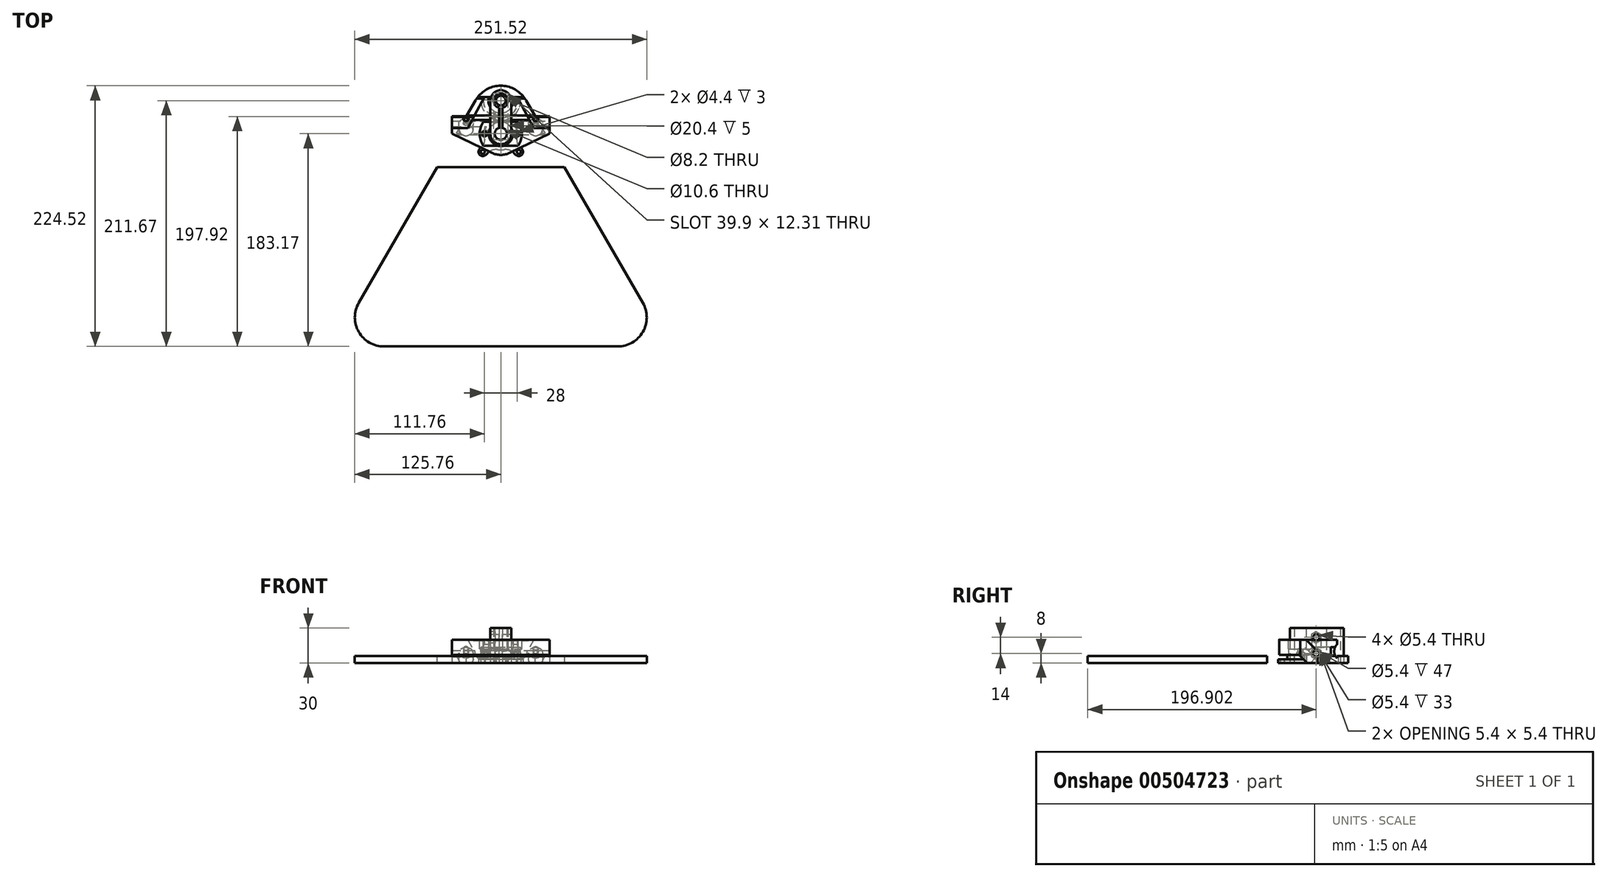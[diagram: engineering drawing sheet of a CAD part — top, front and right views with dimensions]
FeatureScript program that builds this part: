
annotation { "Feature Type Name" : "Feature", "Feature Type Description" : "" }
export const myFeature = defineFeature(function(context is Context, id is Id, definition is map)
    precondition{}
    {
        {
            var Q0;
            Q0=qCreatedBy(makeId("Top.planeOp"),FACE);
            var sketch = newSketch(context, id + "F0", { "sketchPlane" : qUnion([Q0])});
            skCircle(sketch, "E0.cCircle", {"center": v(0, 100) * mm, "radius": 15.5 * mm, "construction": true});
            skLineSegment(sketch, "E0.0", {"start": v(15.5, 115.5) * mm, "end": v(15.5, 84.5) * mm, "construction": true});
            skLineSegment(sketch, "E0.1", {"start": v(15.5, 84.5) * mm, "end": v(-15.5, 84.5) * mm, "construction": true});
            skLineSegment(sketch, "E0.2", {"start": v(-15.5, 84.5) * mm, "end": v(-15.5, 115.5) * mm, "construction": true});
            skLineSegment(sketch, "E0.3", {"start": v(-15.5, 115.5) * mm, "end": v(15.5, 115.5) * mm, "construction": true});
            skPoint(sketch, "E0.0.midPoint", {"position": v(15.5, 100) * mm});
            skCircle(sketch, "E1", {"center": v(0, 100) * mm, "radius": 11.1 * mm});
            skCircle(sketch, "E2", {"center": v(-15.5, 115.5) * mm, "radius": 1.7 * mm});
            skCircle(sketch, "E3", {"center": v(15.5, 115.5) * mm, "radius": 1.7 * mm});
            skCircle(sketch, "E4", {"center": v(15.5, 84.5) * mm, "radius": 1.7 * mm});
            skCircle(sketch, "E5", {"center": v(-15.5, 84.5) * mm, "radius": 1.7 * mm});
            skCircle(sketch, "E6.cCircle", {"center": v(0, 128.5) * mm, "radius": 6.5 * mm, "construction": true});
            skLineSegment(sketch, "E6.0", {"start": v(3.75, 122) * mm, "end": v(-3.75, 122) * mm, "construction": true});
            skLineSegment(sketch, "E6.1", {"start": v(-3.75, 122) * mm, "end": v(-7.5, 128.5) * mm, "construction": true});
            skLineSegment(sketch, "E6.2", {"start": v(-7.5, 128.5) * mm, "end": v(-3.75, 135) * mm, "construction": true});
            skLineSegment(sketch, "E6.3", {"start": v(-3.75, 135) * mm, "end": v(3.75, 135) * mm, "construction": true});
            skLineSegment(sketch, "E6.4", {"start": v(3.75, 135) * mm, "end": v(7.5, 128.5) * mm, "construction": true});
            skLineSegment(sketch, "E6.5", {"start": v(7.5, 128.5) * mm, "end": v(3.75, 122) * mm, "construction": true});
            skPoint(sketch, "E6.0.midPoint", {"position": v(0, 122) * mm});
            skCircle(sketch, "E7", {"center": v(0, 128.5) * mm, "radius": 4.1 * mm});
            skSolve(sketch);
        }
        {
            var Q0;
            Q0=qCreatedBy(makeId("Top.planeOp"),FACE);
            var sketch = newSketch(context, id + "F1", { "sketchPlane" : qUnion([Q0])});
            skCircle(sketch, "E8.cCircle", {"center": v(0, 0) * mm, "radius": 83.17 * mm, "construction": true});
            skLineSegment(sketch, "E8.0", {"start": v(144.06, -83.17) * mm, "end": v(-144.06, -83.17) * mm});
            skLineSegment(sketch, "E8.1", {"start": v(-144.06, -83.17) * mm, "end": v(0, 166.35) * mm});
            skLineSegment(sketch, "E8.2", {"start": v(0, 166.35) * mm, "end": v(144.06, -83.17) * mm});
            skPoint(sketch, "E8.0.midPoint", {"position": v(0, -83.17) * mm});
            skSolve(sketch);
        }
        {
            var Q0;
            Q0=qSketchRegion(id+"F1",true);
            extrude(context, id + "F2", {"entities" : qUnion([Q0]), "depth" : 6 * mm});
        }
        {
            var Q0;
            Q0=qSketchRegion(id+"F0",true);
            extrude(context, id + "F3", {"entities" : qUnion([Q0]), "operationType" : NewBodyOperationType.REMOVE, "endBound" : BoundingType.THROUGH_ALL, "depth" : 25 * mm});
        }
        {
            var Q0;
            Q0=qCreatedBy(makeId("Front.planeOp"),FACE);
            var sketch = newSketch(context, id + "F4", { "sketchPlane" : qUnion([Q0])});
            skLineSegment(sketch, "E9", {"start": v(0, 0) * mm, "end": v(0, 150.06) * mm, "construction": true});
            skSolve(sketch);
        }
        {
            var Q0;
            Q0=makeQuery(id+"F2.opExtrude","SWEPT_EDGE",EDGE,{"disambiguationData":[OSD([sQuery(id+"F1.wireOp",EDGE,"E8.0"),sQuery(id+"F1.wireOp",EDGE,"E8.1")])]});
            var Q1;
            Q1=makeQuery(id+"F2.opExtrude","SWEPT_EDGE",EDGE,{"disambiguationData":[OSD([sQuery(id+"F1.wireOp",EDGE,"E8.0"),sQuery(id+"F1.wireOp",EDGE,"E8.2")])]});
            var Q2;
            Q2=makeQuery(id+"F2.opExtrude","SWEPT_EDGE",EDGE,{"disambiguationData":[OSD([sQuery(id+"F1.wireOp",EDGE,"E8.1"),sQuery(id+"F1.wireOp",EDGE,"E8.2")])]});
            fillet(context, id + "F5", {"entities" : qUnion([Q0, Q1, Q2]), "radius" : 25 * mm, "tangentPropagation" : true, "allowEdgeOverflow" : false});
        }
        {
            var Q0;
            Q0=qCreatedBy(makeId("Top.planeOp"),FACE);
            var sketch = newSketch(context, id + "F6", { "sketchPlane" : qUnion([Q0])});
            skArc(sketch, "E10", {"start": v(-10.2, 131.73) * mm, "mid": v(0, 117.8) * mm, "end": v(10.2, 131.73) * mm});
            skCircle(sketch, "E11", {"center": v(0, 100) * mm, "radius": 10.2 * mm});
            skLineSegment(sketch, "E12", {"start": v(-14, 100) * mm, "end": v(14, 100) * mm, "construction": true});
            skCircle(sketch, "E13", {"center": v(14, 100) * mm, "radius": 2.2 * mm});
            skCircle(sketch, "E14", {"center": v(-14, 100) * mm, "radius": 2.2 * mm});
            skLineSegment(sketch, "E15", {"start": v(-30, 100) * mm, "end": v(30, 100) * mm, "construction": true});
            skArc(sketch, "E16", {"start": v(9.53, 136.9) * mm, "mid": v(0, 141.2) * mm, "end": v(-9.53, 136.9) * mm, "construction": true});
            skLineSegment(sketch, "E17", {"start": v(-30, 100) * mm, "end": v(-42, 100) * mm, "construction": true});
            skLineSegment(sketch, "E18", {"start": v(30, 100) * mm, "end": v(42, 100) * mm, "construction": true});
            skCircle(sketch, "E19", {"center": v(-30, 100) * mm, "radius": 6 * mm, "construction": true});
            skCircle(sketch, "E20", {"center": v(30, 100) * mm, "radius": 6 * mm, "construction": true});
            skLineSegment(sketch, "E21", {"start": v(-14.07, 131.73) * mm, "end": v(-42, 100) * mm, "construction": true});
            skLineSegment(sketch, "E22", {"start": v(14.07, 131.73) * mm, "end": v(42, 100) * mm, "construction": true});
            skArc(sketch, "E23", {"start": v(-7.89, 83.6) * mm, "mid": v(0, 81.8) * mm, "end": v(7.89, 83.6) * mm});
            skLineSegment(sketch, "E24", {"start": v(-7.89, 83.6) * mm, "end": v(-42, 100) * mm});
            skLineSegment(sketch, "E25", {"start": v(42, 100) * mm, "end": v(7.89, 83.6) * mm});
            skLineSegment(sketch, "E26", {"start": v(10.2, 131.73) * mm, "end": v(14.07, 131.73) * mm});
            skLineSegment(sketch, "E27", {"start": v(-10.2, 131.73) * mm, "end": v(-14.07, 131.73) * mm});
            skPoint(sketch, "E28", {"position": v(10.7, 128.5) * mm});
            skLineSegment(sketch, "E29", {"start": v(42, 100) * mm, "end": v(42, 115) * mm});
            skLineSegment(sketch, "E30", {"start": v(42, 115) * mm, "end": v(23, 115) * mm});
            skLineSegment(sketch, "E31", {"start": v(23, 115) * mm, "end": v(14.07, 131.73) * mm});
            skLineSegment(sketch, "E32", {"start": v(-42, 100) * mm, "end": v(-42, 115) * mm});
            skLineSegment(sketch, "E33", {"start": v(-42, 115) * mm, "end": v(-23, 115) * mm});
            skLineSegment(sketch, "E34", {"start": v(-23, 115) * mm, "end": v(-14.07, 131.73) * mm});
            skSolve(sketch);
        }
        {
            var Q0;
            Q0=qSketchRegion(id+"F6",true);
            extrude(context, id + "F7", {"entities" : qUnion([Q0]), "depth" : 20 * mm});
        }
        {
            var Q0;
            Q0=makeQuery(id+"F7.opExtrude","CAP_FACE",FACE,{"disambiguationData":[OSD([sQuery(id+"F6.wireOp",EDGE,"E10"),sQuery(id+"F6.wireOp",EDGE,"E11"),sQuery(id+"F6.wireOp",EDGE,"E13"),sQuery(id+"F6.wireOp",EDGE,"E14"),sQuery(id+"F6.wireOp",EDGE,"E16"),sQuery(id+"F6.wireOp",EDGE,"E21"),sQuery(id+"F6.wireOp",EDGE,"E22"),sQuery(id+"F6.wireOp",EDGE,"E23"),sQuery(id+"F6.wireOp",EDGE,"E24"),sQuery(id+"F6.wireOp",EDGE,"E25")])],"isStart":false});
            var sketch = newSketch(context, id + "F8", { "sketchPlane" : qUnion([Q0])});
            skLineSegment(sketch, "E35", {"start": v(-15.07, 89.8) * mm, "end": v(15.07, 89.8) * mm});
            skLineSegment(sketch, "E36", {"start": v(-15.07, 110.2) * mm, "end": v(15.07, 110.2) * mm});
            skArc(sketch, "E37", {"start": v(-15.07, 110.2) * mm, "mid": v(-18.2, 100) * mm, "end": v(-15.07, 89.8) * mm});
            skArc(sketch, "E38", {"start": v(15.07, 89.8) * mm, "mid": v(18.2, 100) * mm, "end": v(15.07, 110.2) * mm});
            skLineSegment(sketch, "E39", {"start": v(-15.07, 89.8) * mm, "end": v(-15.07, 110.2) * mm, "construction": true});
            skPoint(sketch, "E40", {"position": v(-15.07, 100) * mm});
            skSolve(sketch);
        }
        {
            var Q0;
            Q0=qSketchRegion(id+"F8",true);
            extrude(context, id + "F9", {"entities" : qUnion([Q0]), "operationType" : NewBodyOperationType.REMOVE, "oppositeDirection" : true, "depth" : 8 * mm});
        }
        {
            var Q0;
            Q0=qCreatedBy(makeId("Right.planeOp"),FACE);
            var Q1;
            Q1=sQuery(id+"F6.wireOp",VERTEX,"E18.start");
            cPlane(context, id + "F10", {"entities" : qUnion([Q0, Q1]), "cplaneType" : CPlaneType.PLANE_POINT, "offset" : 25 * mm, "width" : 150 * mm, "height" : 150 * mm});
        }
        {
            var Q0;
            Q0=qCreatedBy(id+"F10.planeOp",FACE);
            var sketch = newSketch(context, id + "F11", { "sketchPlane" : qUnion([Q0])});
            skLineSegment(sketch, "E41", {"start": v(100, 0) * mm, "end": v(100, 22.3) * mm, "construction": true});
            skLineSegment(sketch, "E42", {"start": v(123.17, 29.23) * mm, "end": v(76.83, -17.1) * mm, "construction": true});
            skPoint(sketch, "E43", {"position": v(100, 6.06) * mm});
            skCircle(sketch, "E44", {"center": v(100, 6.06) * mm, "radius": 5 * mm, "construction": true});
            skLineSegment(sketch, "E45", {"start": v(99.34, 11.06) * mm, "end": v(102.07, 11.06) * mm, "construction": true});
            skLineSegment(sketch, "E46", {"start": v(102.07, 11.06) * mm, "end": v(105, 8.13) * mm, "construction": true});
            skLineSegment(sketch, "E47", {"start": v(105, 8.13) * mm, "end": v(105, 5.4) * mm, "construction": true});
            skLineSegment(sketch, "E48", {"start": v(99.34, 11.06) * mm, "end": v(97.93, 12.47) * mm, "construction": true});
            skLineSegment(sketch, "E49", {"start": v(97.93, 12.47) * mm, "end": v(101.46, 16.01) * mm, "construction": true});
            skLineSegment(sketch, "E50", {"start": v(101.46, 16.01) * mm, "end": v(109.95, 7.53) * mm, "construction": true});
            skLineSegment(sketch, "E51", {"start": v(109.95, 7.53) * mm, "end": v(106.41, 3.99) * mm, "construction": true});
            skLineSegment(sketch, "E52", {"start": v(106.41, 3.99) * mm, "end": v(105, 5.4) * mm, "construction": true});
            skLineSegment(sketch, "E53", {"start": v(101.46, 16.01) * mm, "end": v(101.46, 20) * mm, "construction": true});
            skLineSegment(sketch, "E54", {"start": v(106.41, 3.99) * mm, "end": v(106.41, 0) * mm, "construction": true});
            skSolve(sketch);
        }
        {
            var Q0;
            Q0=qCreatedBy(makeId("Right.planeOp"),FACE);
            var sketch = newSketch(context, id + "F12", { "sketchPlane" : qUnion([Q0])});
            skLineSegment(sketch, "E55", {"start": v(106.06, 0) * mm, "end": v(99.06, 7) * mm});
            skLineSegment(sketch, "E56", {"start": v(99.06, 7) * mm, "end": v(71.34, 7) * mm});
            skLineSegment(sketch, "E57", {"start": v(71.34, 7) * mm, "end": v(71.34, 0) * mm});
            skLineSegment(sketch, "E58", {"start": v(71.34, 0) * mm, "end": v(106.06, 0) * mm});
            skSolve(sketch);
        }
        {
            var Q0;
            Q0=qSketchRegion(id+"F12",true);
            extrude(context, id + "F13", {"entities" : qUnion([Q0]), "operationType" : NewBodyOperationType.REMOVE, "endBound" : BoundingType.THROUGH_ALL, "oppositeDirection" : true, "depth" : 25 * mm, "hasSecondDirection" : true, "secondDirectionBound" : SecondDirectionBoundingType.THROUGH_ALL, "secondDirectionOppositeDirection" : false, "secondDirectionDepth" : 25 * mm});
        }
        {
            var Q0;
            Q0=sQuery(id+"F11.wireOp",EDGE,"E50");
            cPoint(context, id + "F14", {"entities" : qUnion([Q0]), "parameter" : 0.5});
        }
        {
            var Q0;
            Q0=qCreatedBy(id+"F14",VERTEX);
            var Q1;
            Q1=sQuery(id+"F11.wireOp",EDGE,"E42");
            cPlane(context, id + "F15", {"entities" : qUnion([Q0, Q1]), "cplaneType" : CPlaneType.LINE_POINT, "offset" : 25 * mm, "width" : 150 * mm, "height" : 150 * mm});
        }
        {
            var Q0;
            Q0=qCreatedBy(id+"F15.planeOp",FACE);
            var sketch = newSketch(context, id + "F16", { "sketchPlane" : qUnion([Q0])});
            skCircle(sketch, "E59", {"center": v(30, -70.71) * mm, "radius": 6.2 * mm});
            skCircle(sketch, "E60", {"center": v(-30, -70.71) * mm, "radius": 6.2 * mm});
            skSolve(sketch);
        }
        {
            var Q0;
            Q0=qSketchRegion(id+"F16",true);
            extrude(context, id + "F17", {"entities" : qUnion([Q0]), "operationType" : NewBodyOperationType.REMOVE, "endBound" : BoundingType.THROUGH_ALL, "depth" : 25 * mm});
        }
        {
            var Q0;
            Q0=makeQuery(id+"F7.opExtrude","CAP_EDGE",EDGE,{"disambiguationData":[OSD([sQuery(id+"F6.wireOp",EDGE,"E30")])],"isStart":false});
            var Q1;
            Q1=makeQuery(id+"F7.opExtrude","CAP_EDGE",EDGE,{"disambiguationData":[OSD([sQuery(id+"F6.wireOp",EDGE,"E33")])],"isStart":false});
            chamfer(context, id + "F18", {"entities" : qUnion([Q0, Q1]), "width" : 10 * mm, "tangentPropagation" : true});
        }
        {
            var Q0;
            Q0=qCreatedBy(id+"F15.planeOp",FACE);
            var sketch = newSketch(context, id + "F19", { "sketchPlane" : qUnion([Q0])});
            skCircle(sketch, "E61", {"center": v(-30, -70.71) * mm, "radius": 2.2 * mm});
            skCircle(sketch, "E62", {"center": v(30, -70.71) * mm, "radius": 2.2 * mm});
            skSolve(sketch);
        }
        {
            var Q0;
            Q0=qSketchRegion(id+"F19",true);
            extrude(context, id + "F20", {"entities" : qUnion([Q0]), "operationType" : NewBodyOperationType.REMOVE, "endBound" : BoundingType.THROUGH_ALL, "oppositeDirection" : true, "depth" : 25 * mm});
        }
        {
            var Q0;
            Q0=qCreatedBy(makeId("Right.planeOp"),FACE);
            var sketch = newSketch(context, id + "F21", { "sketchPlane" : qUnion([Q0])});
            skArc(sketch, "E63", {"start": v(131.73, 16) * mm, "mid": v(129.25, 10) * mm, "end": v(131.73, 4) * mm});
            skLineSegment(sketch, "E64", {"start": v(131.73, 16) * mm, "end": v(131.73, 4) * mm});
            skLineSegment(sketch, "E65", {"start": v(131.73, 16) * mm, "end": v(131.73, 20) * mm, "construction": true});
            skLineSegment(sketch, "E66", {"start": v(131.73, 4) * mm, "end": v(131.73, 0) * mm, "construction": true});
            skLineSegment(sketch, "E67", {"start": v(137.73, 10) * mm, "end": v(131.73, 16) * mm, "construction": true});
            skSolve(sketch);
        }
        {
            var Q0;
            Q0=qSketchRegion(id+"F21",true);
            extrude(context, id + "F22", {"entities" : qUnion([Q0]), "operationType" : NewBodyOperationType.REMOVE, "endBound" : BoundingType.THROUGH_ALL, "oppositeDirection" : true, "depth" : 25 * mm, "hasSecondDirection" : true, "secondDirectionBound" : SecondDirectionBoundingType.THROUGH_ALL, "secondDirectionOppositeDirection" : false, "secondDirectionDepth" : 25 * mm});
        }
        {
            var Q0;
            Q0=makeQuery(id+"F13.boolean.opBoolean","COPY",FACE,{"derivedFrom":makeQuery(id+"F13.opExtrude","SWEPT_FACE",FACE,{"disambiguationData":[OSD([sQuery(id+"F12.wireOp",EDGE,"E56")])]})});
            var sketch = newSketch(context, id + "F23", { "sketchPlane" : qUnion([Q0])});
            skCircle(sketch, "E68.cCircle", {"center": v(14, -100) * mm, "radius": 2.9 * mm, "construction": true});
            skLineSegment(sketch, "E68.0", {"start": v(14, -103.35) * mm, "end": v(11.1, -101.67) * mm});
            skLineSegment(sketch, "E68.1", {"start": v(11.1, -101.67) * mm, "end": v(11.1, -98.33) * mm});
            skLineSegment(sketch, "E68.2", {"start": v(11.1, -98.33) * mm, "end": v(14, -96.65) * mm});
            skLineSegment(sketch, "E68.3", {"start": v(14, -96.65) * mm, "end": v(16.9, -98.33) * mm});
            skLineSegment(sketch, "E68.4", {"start": v(16.9, -98.33) * mm, "end": v(16.9, -101.67) * mm});
            skLineSegment(sketch, "E68.5", {"start": v(16.9, -101.67) * mm, "end": v(14, -103.35) * mm});
            skPoint(sketch, "E68.0.midPoint", {"position": v(12.55, -102.51) * mm});
            skCircle(sketch, "E69.cCircle", {"center": v(-14, -100) * mm, "radius": 2.9 * mm, "construction": true});
            skLineSegment(sketch, "E69.0", {"start": v(-14, -103.35) * mm, "end": v(-16.9, -101.67) * mm});
            skLineSegment(sketch, "E69.1", {"start": v(-16.9, -101.67) * mm, "end": v(-16.9, -98.33) * mm});
            skLineSegment(sketch, "E69.2", {"start": v(-16.9, -98.33) * mm, "end": v(-14, -96.65) * mm});
            skLineSegment(sketch, "E69.3", {"start": v(-14, -96.65) * mm, "end": v(-11.1, -98.33) * mm});
            skLineSegment(sketch, "E69.4", {"start": v(-11.1, -98.33) * mm, "end": v(-11.1, -101.67) * mm});
            skLineSegment(sketch, "E69.5", {"start": v(-11.1, -101.67) * mm, "end": v(-14, -103.35) * mm});
            skPoint(sketch, "E69.0.midPoint", {"position": v(-15.45, -102.51) * mm});
            skSolve(sketch);
        }
        {
            var Q0;
            Q0=qSketchRegion(id+"F23",true);
            extrude(context, id + "F24", {"entities" : qUnion([Q0]), "operationType" : NewBodyOperationType.REMOVE, "oppositeDirection" : true, "depth" : 2 * mm, "hasSecondDirection" : true, "secondDirectionBound" : SecondDirectionBoundingType.THROUGH_ALL, "secondDirectionOppositeDirection" : false, "secondDirectionDepth" : 25 * mm});
        }
        {
            var Q0;
            Q0=qCreatedBy(makeId("Right.planeOp"),FACE);
            var sketch = newSketch(context, id + "F25", { "sketchPlane" : qUnion([Q0])});
            skLineSegment(sketch, "E70", {"start": v(128.5, 0) * mm, "end": v(128.5, 20) * mm, "construction": true});
            skLineSegment(sketch, "E71.bottom", {"start": v(111.5, 13.5) * mm, "end": v(113.5, 13.5) * mm});
            skLineSegment(sketch, "E71.top", {"start": v(111.5, 6.5) * mm, "end": v(113.5, 6.5) * mm});
            skLineSegment(sketch, "E71.left", {"start": v(111.5, 13.5) * mm, "end": v(111.5, 6.5) * mm});
            skLineSegment(sketch, "E71.right", {"start": v(113.5, 13.5) * mm, "end": v(113.5, 6.5) * mm});
            skLineSegment(sketch, "E72", {"start": v(113.5, 10) * mm, "end": v(128.5, 10) * mm, "construction": true});
            skSolve(sketch);
        }
        {
            var Q0;
            Q0=qSketchRegion(id+"F25",true);
            var Q1;
            Q1=sQuery(id+"F25.wireOp",EDGE,"E70");
            revolve(context, id + "F26", {"operationType" : NewBodyOperationType.REMOVE, "entities" : qUnion([Q0]), "axis" : qUnion([Q1]), "revolveType" : RevolveType.FULL, "oppositeDirection" : true});
        }
        {
            var Q0;
            Q0=qCreatedBy(makeId("Top.planeOp"),FACE);
            var sketch = newSketch(context, id + "F27", { "sketchPlane" : qUnion([Q0])});
            skCircle(sketch, "E73", {"center": v(0, 100) * mm, "radius": 5.3 * mm});
            skCircle(sketch, "E74", {"center": v(-15.5, 115.5) * mm, "radius": 1.7 * mm});
            skCircle(sketch, "E75", {"center": v(15.5, 115.5) * mm, "radius": 1.7 * mm});
            skCircle(sketch, "E76", {"center": v(15.5, 84.5) * mm, "radius": 1.7 * mm});
            skCircle(sketch, "E77", {"center": v(-15.5, 84.5) * mm, "radius": 1.7 * mm});
            skArc(sketch, "E78", {"start": v(18.12, 112.88) * mm, "mid": v(18.12, 118.12) * mm, "end": v(12.88, 118.12) * mm});
            skCircle(sketch, "E79", {"center": v(0, 100) * mm, "radius": 11 * mm});
            skArc(sketch, "E80", {"start": v(6.93, 112.16) * mm, "mid": v(0, 114) * mm, "end": v(-6.93, 112.16) * mm});
            skArc(sketch, "E81", {"start": v(-12.88, 118.12) * mm, "mid": v(-18.12, 118.12) * mm, "end": v(-18.12, 112.88) * mm});
            skArc(sketch, "E82", {"start": v(-18.12, 87.12) * mm, "mid": v(-18.12, 81.88) * mm, "end": v(-12.88, 81.88) * mm});
            skArc(sketch, "E83", {"start": v(12.88, 81.88) * mm, "mid": v(18.12, 81.88) * mm, "end": v(18.12, 87.12) * mm});
            skArc(sketch, "E84", {"start": v(-6.93, 87.84) * mm, "mid": v(0, 86) * mm, "end": v(6.93, 87.84) * mm});
            skArc(sketch, "E85", {"start": v(-12.16, 106.93) * mm, "mid": v(-14, 100) * mm, "end": v(-12.16, 93.07) * mm});
            skArc(sketch, "E86", {"start": v(12.16, 93.07) * mm, "mid": v(14, 100) * mm, "end": v(12.16, 106.93) * mm});
            skLineSegment(sketch, "E87", {"start": v(12.88, 81.88) * mm, "end": v(6.93, 87.84) * mm});
            skLineSegment(sketch, "E88", {"start": v(-6.93, 87.84) * mm, "end": v(-12.88, 81.88) * mm});
            skLineSegment(sketch, "E89", {"start": v(-18.12, 87.12) * mm, "end": v(-12.16, 93.07) * mm});
            skLineSegment(sketch, "E90", {"start": v(-12.16, 106.93) * mm, "end": v(-18.12, 112.88) * mm});
            skLineSegment(sketch, "E91", {"start": v(-12.88, 118.12) * mm, "end": v(-6.93, 112.16) * mm});
            skLineSegment(sketch, "E92", {"start": v(18.12, 87.12) * mm, "end": v(12.16, 93.07) * mm});
            skLineSegment(sketch, "E93", {"start": v(6.93, 112.16) * mm, "end": v(12.88, 118.12) * mm});
            skLineSegment(sketch, "E94", {"start": v(12.16, 106.93) * mm, "end": v(18.12, 112.88) * mm});
            skSolve(sketch);
        }
        {
            var Q0;
            Q0=qSketchRegion(id+"F27",true);
            var Q1;
            Q1=makeQuery(id+"F27.imprint","IMPRINT",FACE,{"disambiguationData":[TD([[makeQuery(id+"F27.imprint","IMPRINT",EDGE,{"derivedFrom":sQuery(id+"F27.wireOp",EDGE,"E73")}),-1.0]])]});
            extrude(context, id + "F28", {"entities" : qUnion([Q0, Q1]), "depth" : 3 * mm});
        }
        {
            var Q0;
            Q0=makeQuery(id+"F27.imprint","IMPRINT",FACE,{"disambiguationData":[TD([[makeQuery(id+"F27.imprint","IMPRINT",EDGE,{"derivedFrom":sQuery(id+"F27.wireOp",EDGE,"E73")}),1.0]])]});
            var Q1;
            Q1=makeQuery(id+"F0.imprint","IMPRINT",FACE,{"disambiguationData":[TD([[makeQuery(id+"F0.imprint","IMPRINT",EDGE,{"derivedFrom":sQuery(id+"F0.wireOp",EDGE,"E1")}),1.0]])]});
            extrude(context, id + "F29", {"entities" : qUnion([Q0, Q1]), "operationType" : NewBodyOperationType.ADD, "depth" : 7 * mm});
        }
        {
            var Q0;
            Q0=makeQuery(id+"F27.imprint","IMPRINT",FACE,{"disambiguationData":[TD([[makeQuery(id+"F27.imprint","IMPRINT",EDGE,{"derivedFrom":sQuery(id+"F27.wireOp",EDGE,"E73")}),1.0]])]});
            var Q1;
            Q1=sQuery(id+"F27.wireOp",EDGE,"E73");
            extrude(context, id + "F30", {"entities" : qUnion([Q0]), "operationType" : NewBodyOperationType.REMOVE, "surfaceEntities" : qUnion([Q1]), "endBound" : BoundingType.THROUGH_ALL, "depth" : 25 * mm});
        }
        {
            var Q0;
            Q0=makeQuery(id+"F28.opExtrude","SWEPT_EDGE",EDGE,{"disambiguationData":[OSD([sQuery(id+"F27.wireOp",EDGE,"E84"),sQuery(id+"F27.wireOp",EDGE,"E88")])]});
            var Q1;
            Q1=makeQuery(id+"F28.opExtrude","SWEPT_EDGE",EDGE,{"disambiguationData":[OSD([sQuery(id+"F27.wireOp",EDGE,"E84"),sQuery(id+"F27.wireOp",EDGE,"E87")])]});
            var Q2;
            Q2=makeQuery(id+"F28.opExtrude","SWEPT_EDGE",EDGE,{"disambiguationData":[OSD([sQuery(id+"F27.wireOp",EDGE,"E86"),sQuery(id+"F27.wireOp",EDGE,"E94")])]});
            var Q3;
            Q3=makeQuery(id+"F28.opExtrude","SWEPT_EDGE",EDGE,{"disambiguationData":[OSD([sQuery(id+"F27.wireOp",EDGE,"E86"),sQuery(id+"F27.wireOp",EDGE,"E92")])]});
            var Q4;
            Q4=makeQuery(id+"F28.opExtrude","SWEPT_EDGE",EDGE,{"disambiguationData":[OSD([sQuery(id+"F27.wireOp",EDGE,"E80"),sQuery(id+"F27.wireOp",EDGE,"E93")])]});
            var Q5;
            Q5=makeQuery(id+"F28.opExtrude","SWEPT_EDGE",EDGE,{"disambiguationData":[OSD([sQuery(id+"F27.wireOp",EDGE,"E80"),sQuery(id+"F27.wireOp",EDGE,"E91")])]});
            var Q6;
            Q6=makeQuery(id+"F28.opExtrude","SWEPT_EDGE",EDGE,{"disambiguationData":[OSD([sQuery(id+"F27.wireOp",EDGE,"E85"),sQuery(id+"F27.wireOp",EDGE,"E90")])]});
            var Q7;
            Q7=makeQuery(id+"F28.opExtrude","SWEPT_EDGE",EDGE,{"disambiguationData":[OSD([sQuery(id+"F27.wireOp",EDGE,"E85"),sQuery(id+"F27.wireOp",EDGE,"E89")])]});
            fillet(context, id + "F31", {"entities" : qUnion([Q0, Q1, Q2, Q3, Q4, Q5, Q6, Q7]), "radius" : 10 * mm, "tangentPropagation" : true, "allowEdgeOverflow" : false});
        }
        {
            var Q0;
            Q0=qCreatedBy(makeId("Top.planeOp"),FACE);
            var sketch = newSketch(context, id + "F32", { "sketchPlane" : qUnion([Q0])});
            skArc(sketch, "E95", {"start": v(1.5, 122.48) * mm, "mid": v(0, 134.7) * mm, "end": v(-1.5, 122.48) * mm});
            skArc(sketch, "E96", {"start": v(-1.5, 104.98) * mm, "mid": v(0, 94.8) * mm, "end": v(1.5, 104.98) * mm});
            skArc(sketch, "E97", {"start": v(-9, 128.5) * mm, "mid": v(0, 137.5) * mm, "end": v(9, 128.5) * mm});
            skArc(sketch, "E98", {"start": v(-9, 100) * mm, "mid": v(0, 91) * mm, "end": v(9, 100) * mm});
            skLineSegment(sketch, "E99", {"start": v(9, 100) * mm, "end": v(9, 128.5) * mm});
            skLineSegment(sketch, "E100", {"start": v(-9, 128.5) * mm, "end": v(-9, 100) * mm});
            skLineSegment(sketch, "E101", {"start": v(-1.5, 122.48) * mm, "end": v(-1.5, 104.98) * mm});
            skLineSegment(sketch, "E102", {"start": v(1.5, 122.48) * mm, "end": v(1.5, 104.98) * mm});
            skSolve(sketch);
        }
        {
            var Q0;
            Q0=qSketchRegion(id+"F32",true);
            extrude(context, id + "F33", {"entities" : qUnion([Q0]), "depth" : 30 * mm});
        }
        {
            var Q0;
            Q0=qCreatedBy(makeId("Right.planeOp"),FACE);
            var sketch = newSketch(context, id + "F34", { "sketchPlane" : qUnion([Q0])});
            skCircle(sketch, "E103", {"center": v(113.73, 22) * mm, "radius": 2.7 * mm});
            skLineSegment(sketch, "E104", {"start": v(113.73, 30) * mm, "end": v(113.73, 22) * mm, "construction": true});
            skLineSegment(sketch, "E105", {"start": v(113.73, 22) * mm, "end": v(113.73, 8) * mm, "construction": true});
            skLineSegment(sketch, "E106", {"start": v(113.73, 8) * mm, "end": v(113.73, 0) * mm, "construction": true});
            skCircle(sketch, "E107", {"center": v(113.73, 8) * mm, "radius": 2.7 * mm});
            skSolve(sketch);
        }
        {
            var Q0;
            Q0=qSketchRegion(id+"F34",true);
            extrude(context, id + "F35", {"entities" : qUnion([Q0]), "operationType" : NewBodyOperationType.REMOVE, "endBound" : BoundingType.THROUGH_ALL, "oppositeDirection" : true, "depth" : 25 * mm, "hasSecondDirection" : true, "secondDirectionBound" : SecondDirectionBoundingType.THROUGH_ALL, "secondDirectionOppositeDirection" : false, "secondDirectionDepth" : 25 * mm});
        }
        {
            var Q0;
            Q0=makeQuery(id+"F33.opExtrude","SWEPT_FACE",FACE,{"disambiguationData":[OSD([sQuery(id+"F32.wireOp",EDGE,"E100")])]});
            var sketch = newSketch(context, id + "F36", { "sketchPlane" : qUnion([Q0])});
            skCircle(sketch, "E108.cCircle", {"center": v(-113.73, 22) * mm, "radius": 4.2 * mm, "construction": true});
            skLineSegment(sketch, "E108.0", {"start": v(-109.53, 24.42) * mm, "end": v(-109.53, 19.58) * mm});
            skLineSegment(sketch, "E108.1", {"start": v(-109.53, 19.58) * mm, "end": v(-113.73, 17.15) * mm});
            skLineSegment(sketch, "E108.2", {"start": v(-113.73, 17.15) * mm, "end": v(-117.93, 19.58) * mm});
            skLineSegment(sketch, "E108.3", {"start": v(-117.93, 19.58) * mm, "end": v(-117.93, 24.42) * mm});
            skLineSegment(sketch, "E108.4", {"start": v(-117.93, 24.42) * mm, "end": v(-113.73, 26.85) * mm});
            skLineSegment(sketch, "E108.5", {"start": v(-113.73, 26.85) * mm, "end": v(-109.53, 24.42) * mm});
            skPoint(sketch, "E108.0.midPoint", {"position": v(-109.53, 22) * mm});
            skCircle(sketch, "E109.cCircle", {"center": v(-113.73, 8) * mm, "radius": 4.2 * mm, "construction": true});
            skLineSegment(sketch, "E109.0", {"start": v(-109.53, 10.42) * mm, "end": v(-109.53, 5.58) * mm});
            skLineSegment(sketch, "E109.1", {"start": v(-109.53, 5.58) * mm, "end": v(-113.73, 3.15) * mm});
            skLineSegment(sketch, "E109.2", {"start": v(-113.73, 3.15) * mm, "end": v(-117.93, 5.58) * mm});
            skLineSegment(sketch, "E109.3", {"start": v(-117.93, 5.58) * mm, "end": v(-117.93, 10.42) * mm});
            skLineSegment(sketch, "E109.4", {"start": v(-117.93, 10.42) * mm, "end": v(-113.73, 12.85) * mm});
            skLineSegment(sketch, "E109.5", {"start": v(-113.73, 12.85) * mm, "end": v(-109.53, 10.42) * mm});
            skPoint(sketch, "E109.0.midPoint", {"position": v(-109.53, 8) * mm});
            skSolve(sketch);
        }
        {
            var Q0;
            Q0=qSketchRegion(id+"F36",true);
            extrude(context, id + "F37", {"entities" : qUnion([Q0]), "operationType" : NewBodyOperationType.REMOVE, "oppositeDirection" : true, "depth" : 4 * mm});
        }
    });
